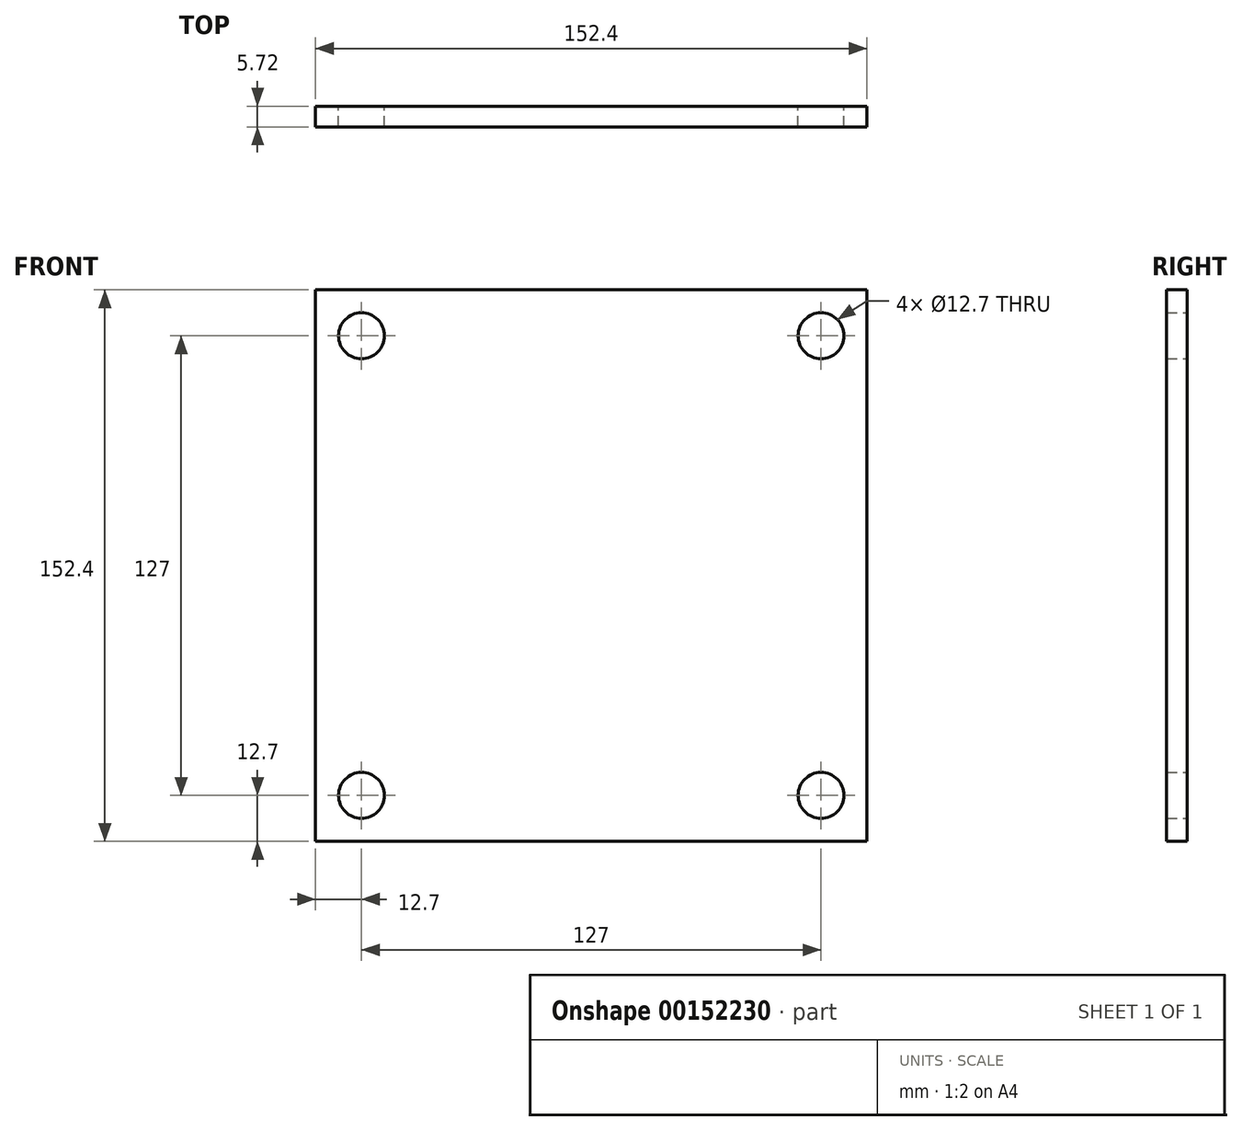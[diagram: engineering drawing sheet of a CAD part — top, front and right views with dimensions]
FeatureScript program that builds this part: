
annotation { "Feature Type Name" : "Feature", "Feature Type Description" : "" }
export const myFeature = defineFeature(function(context is Context, id is Id, definition is map)
    precondition{}
    {
        {
            var Q0;
            Q0=qCreatedBy(makeId("Front.planeOp"),FACE);
            var sketch = newSketch(context, id + "F0", { "sketchPlane" : qUnion([Q0])});
            skCircle(sketch, "E0", {"center": v(-63.5, 63.5) * mm, "radius": 6.35 * mm});
            skCircle(sketch, "E1", {"center": v(63.5, 63.5) * mm, "radius": 6.35 * mm});
            skCircle(sketch, "E2", {"center": v(63.5, -63.5) * mm, "radius": 6.35 * mm});
            skCircle(sketch, "E3", {"center": v(-63.5, -63.5) * mm, "radius": 6.35 * mm});
            skLineSegment(sketch, "E4", {"start": v(-63.5, 63.5) * mm, "end": v(-63.5, -63.5) * mm, "construction": true});
            skLineSegment(sketch, "E5", {"start": v(-63.5, -63.5) * mm, "end": v(63.5, -63.5) * mm, "construction": true});
            skLineSegment(sketch, "E6", {"start": v(63.5, -63.5) * mm, "end": v(63.5, 63.5) * mm, "construction": true});
            skLineSegment(sketch, "E7", {"start": v(63.5, 63.5) * mm, "end": v(-63.5, 63.5) * mm, "construction": true});
            skLineSegment(sketch, "E8", {"start": v(0, 63.5) * mm, "end": v(0, 0) * mm, "construction": true});
            skLineSegment(sketch, "E9", {"start": v(-63.5, 0) * mm, "end": v(0, 0) * mm, "construction": true});
            skLineSegment(sketch, "E10.bottom", {"start": v(-76.2, 76.2) * mm, "end": v(76.2, 76.2) * mm});
            skLineSegment(sketch, "E10.top", {"start": v(-76.2, -76.2) * mm, "end": v(76.2, -76.2) * mm});
            skLineSegment(sketch, "E10.left", {"start": v(-76.2, 76.2) * mm, "end": v(-76.2, -76.2) * mm});
            skLineSegment(sketch, "E10.right", {"start": v(76.2, 76.2) * mm, "end": v(76.2, -76.2) * mm});
            skPoint(sketch, "E10.middle", {"position": v(0, 0) * mm});
            skSolve(sketch);
        }
        {
            var Q0;
            Q0=makeQuery(id+"F0.imprint","IMPRINT",FACE,{"disambiguationData":[TD([[makeQuery(id+"F0.imprint","IMPRINT",EDGE,{"derivedFrom":sQuery(id+"F0.wireOp",EDGE,"E0")}),-1.0]])]});
            extrude(context, id + "F1", {"entities" : qUnion([Q0]), "depth" : 5.7 * mm});
        }
    });
